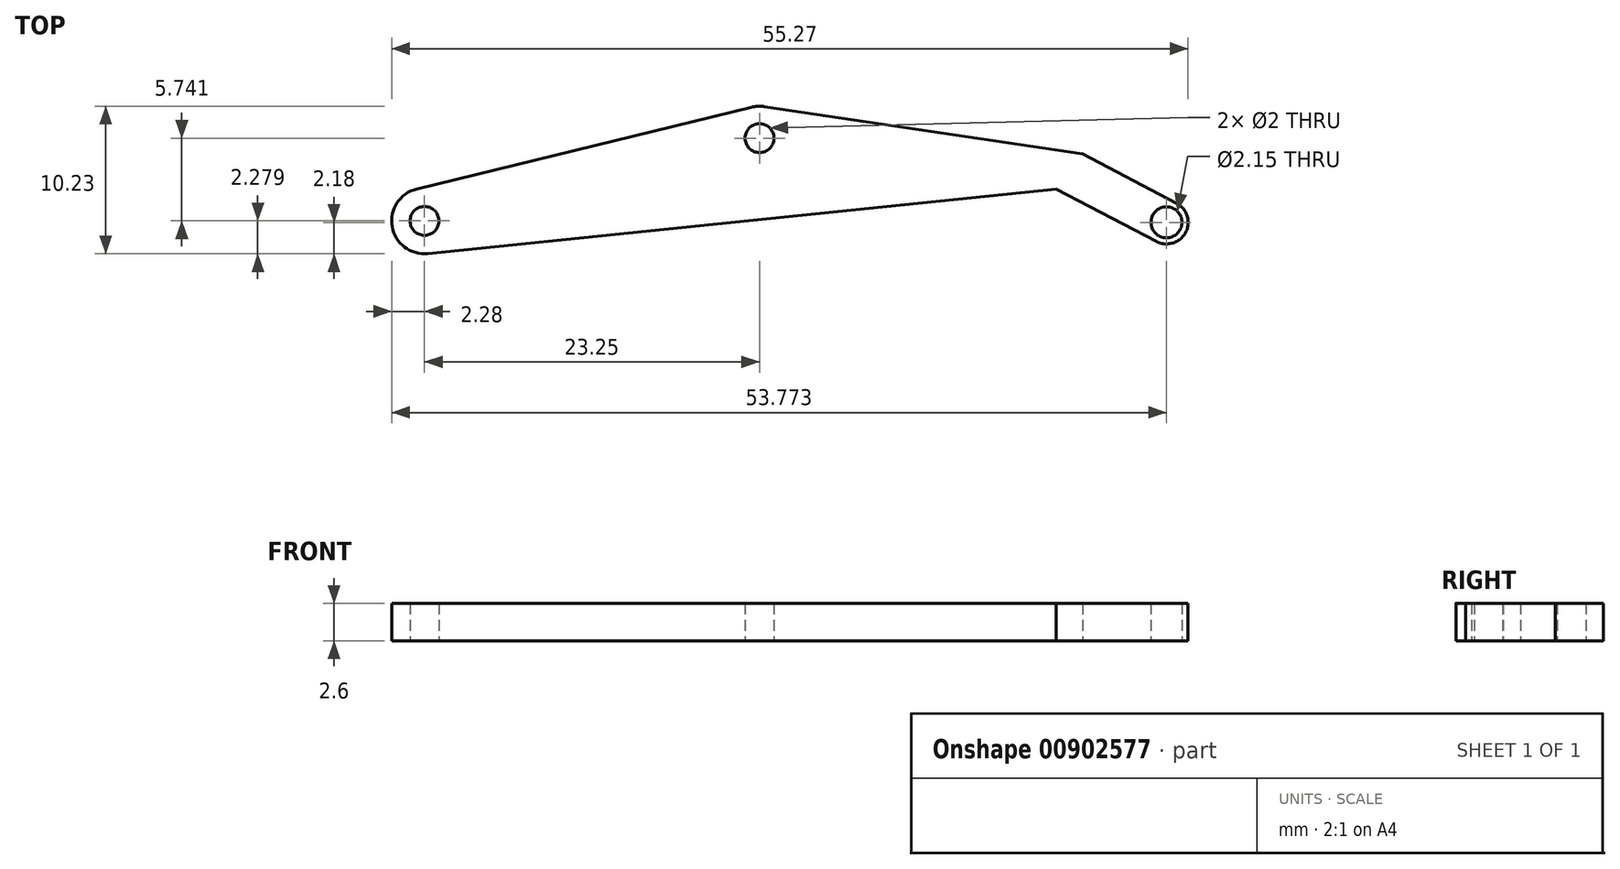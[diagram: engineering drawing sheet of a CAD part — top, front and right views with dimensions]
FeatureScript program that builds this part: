
annotation { "Feature Type Name" : "Feature", "Feature Type Description" : "" }
export const myFeature = defineFeature(function(context is Context, id is Id, definition is map)
    precondition{}
    {
        {
            var Q0;
            Q0=qCreatedBy(makeId("Top.planeOp"),FACE);
            var sketch = newSketch(context, id + "F0", { "sketchPlane" : qUnion([Q0])});
            skCircle(sketch, "E0", {"center": v(-1.2, 3.05) * mm, "radius": 2.21 * mm});
            skCircle(sketch, "E1", {"center": v(-24.45, -2.7) * mm, "radius": 2.28 * mm});
            skCircle(sketch, "E2", {"center": v(27.04, -2.79) * mm, "radius": 1.5 * mm});
            skLineSegment(sketch, "E3", {"start": v(-25, -0.48) * mm, "end": v(-1.72, 5.2) * mm});
            skLineSegment(sketch, "E4", {"start": v(21.22, 1.95) * mm, "end": v(27.74, -1.46) * mm});
            skLineSegment(sketch, "E5", {"start": v(-24.22, -4.96) * mm, "end": v(19.37, -0.47) * mm});
            skLineSegment(sketch, "E6", {"start": v(19.37, -0.47) * mm, "end": v(26.35, -4.12) * mm});
            skLineSegment(sketch, "E7", {"start": v(21.22, 1.95) * mm, "end": v(-0.87, 5.24) * mm});
            skCircle(sketch, "E8", {"center": v(-24.45, -2.7) * mm, "radius": 1 * mm});
            skCircle(sketch, "E9", {"center": v(-1.2, 3.05) * mm, "radius": 1 * mm});
            skCircle(sketch, "E10", {"center": v(27.04, -2.79) * mm, "radius": 1.07 * mm});
            skSolve(sketch);
        }
        {
            var Q0;
            Q0=qSketchRegion(id+"F0",true);
            extrude(context, id + "F1", {"entities" : qUnion([Q0]), "depth" : 1.3 * mm, "offsetDistance" : 25 * mm});
        }
        {
            var Q0;
            Q0=makeQuery(id+"F1.opExtrude","SWEPT_BODY",BODY,{"disambiguationData":[OSD([sQuery(id+"F0.wireOp",EDGE,"E0"),sQuery(id+"F0.wireOp",EDGE,"E1"),sQuery(id+"F0.wireOp",EDGE,"E2"),sQuery(id+"F0.wireOp",EDGE,"E3"),sQuery(id+"F0.wireOp",EDGE,"E4"),sQuery(id+"F0.wireOp",EDGE,"E5"),sQuery(id+"F0.wireOp",EDGE,"E6"),sQuery(id+"F0.wireOp",EDGE,"E7"),sQuery(id+"F0.wireOp",EDGE,"E8"),sQuery(id+"F0.wireOp",EDGE,"E9")])]});
            var Q1;
            Q1=qCreatedBy(makeId("Top.planeOp"),FACE);
            mirror(context, id + "F2", {"operationType" : NewBodyOperationType.ADD, "entities" : qUnion([Q0]), "mirrorPlane" : qUnion([Q1])});
        }
    });
